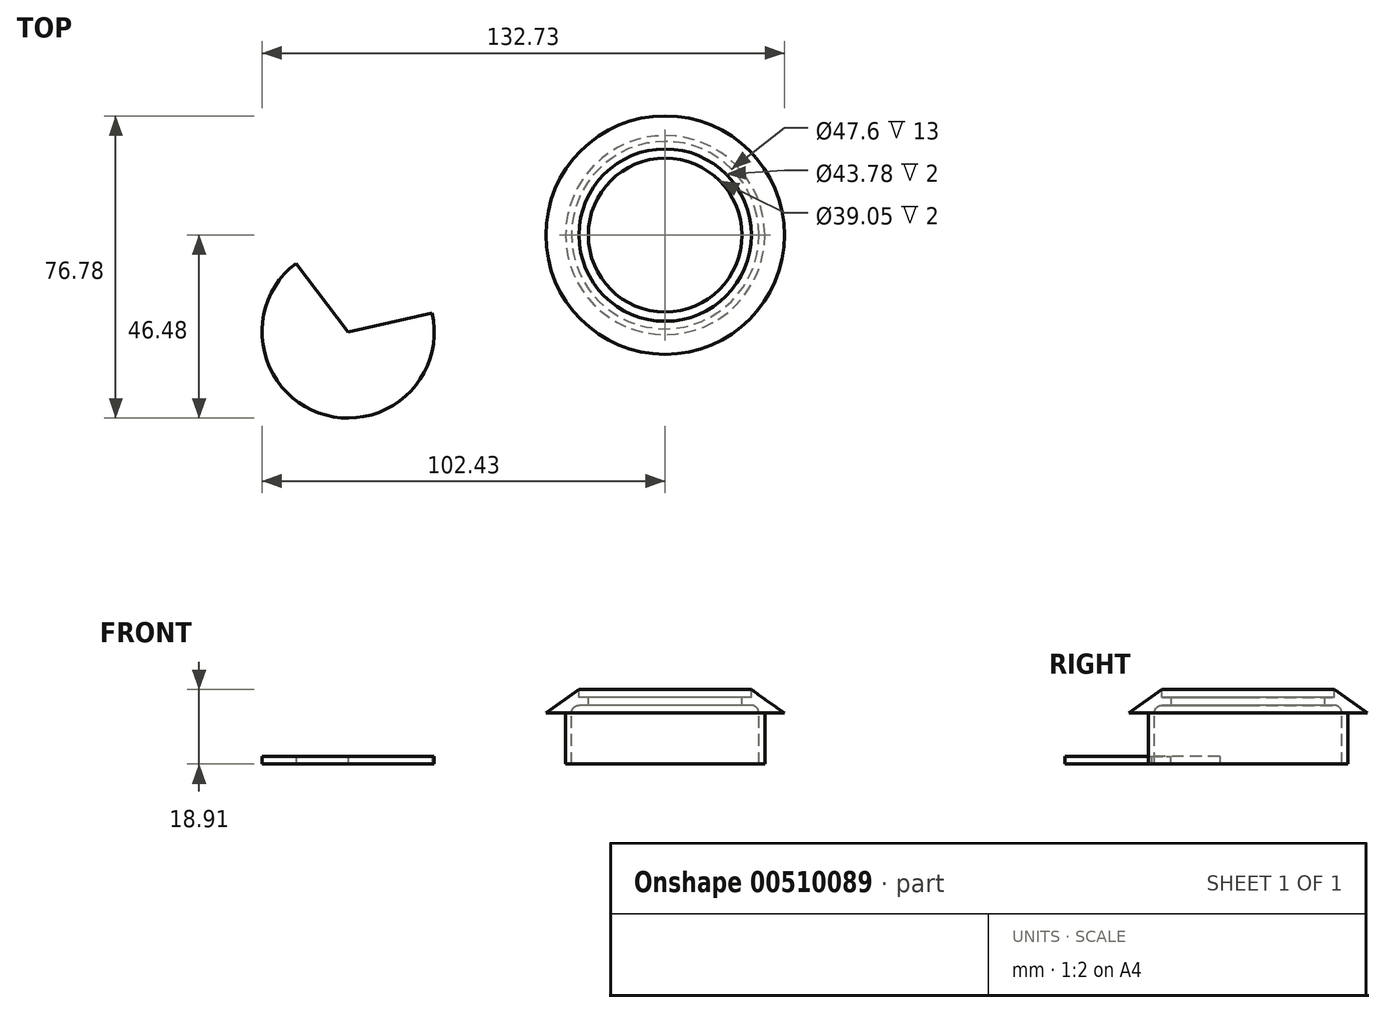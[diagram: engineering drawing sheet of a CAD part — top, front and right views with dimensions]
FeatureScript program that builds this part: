
annotation { "Feature Type Name" : "Feature", "Feature Type Description" : "" }
export const myFeature = defineFeature(function(context is Context, id is Id, definition is map)
    precondition{}
    {
        {
            var Q0;
            Q0=qCreatedBy(makeId("Front.planeOp"),FACE);
            var sketch = newSketch(context, id + "F0", { "sketchPlane" : qUnion([Q0])});
            skLineSegment(sketch, "E0", {"start": v(23.8, 0) * mm, "end": v(25.3, 0) * mm});
            skLineSegment(sketch, "E1", {"start": v(25.3, 0) * mm, "end": v(25.3, 13) * mm});
            skLineSegment(sketch, "E2", {"start": v(25.3, 13) * mm, "end": v(30.3, 13) * mm});
            skLineSegment(sketch, "E3", {"start": v(30.3, 13) * mm, "end": v(21.89, 18.91) * mm});
            skLineSegment(sketch, "E4", {"start": v(21.89, 18.91) * mm, "end": v(21.89, 16.91) * mm});
            skLineSegment(sketch, "E5", {"start": v(21.89, 16.91) * mm, "end": v(19.53, 16.91) * mm});
            skLineSegment(sketch, "E6", {"start": v(23.8, 0) * mm, "end": v(23.8, 13) * mm});
            skLineSegment(sketch, "E7", {"start": v(0, 10.58) * mm, "end": v(0, -2.42) * mm, "construction": true});
            skLineSegment(sketch, "E8", {"start": v(19.53, 16.91) * mm, "end": v(19.53, 14.91) * mm});
            skLineSegment(sketch, "E9", {"start": v(19.53, 14.91) * mm, "end": v(21.89, 14.91) * mm});
            skArc(sketch, "E10", {"start": v(23.8, 13) * mm, "mid": v(23.24, 14.35) * mm, "end": v(21.89, 14.91) * mm});
            skSolve(sketch);
        }
        {
            var Q0;
            Q0 = qSketchRegion(id + "F0", true);
            var Q1;
            Q1=sQuery(id+"F0.wireOp",EDGE,"E7");
            revolve(context, id + "F1", {"entities" : qUnion([Q0]), "axis" : qUnion([Q1]), "revolveType" : RevolveType.FULL});
        }
        {
            var Q0;
            Q0=qCreatedBy(makeId("Top.planeOp"),FACE);
            var sketch = newSketch(context, id + "F2", { "sketchPlane" : qUnion([Q0])});
            skArc(sketch, "E11", {"start": v(-93.81, -7.2) * mm, "mid": v(-88, -45.17) * mm, "end": v(-59.2, -19.74) * mm});
            skLineSegment(sketch, "E12", {"start": v(-93.81, -7.2) * mm, "end": v(-80.54, -24.6) * mm});
            skLineSegment(sketch, "E13", {"start": v(-80.54, -24.6) * mm, "end": v(-59.2, -19.74) * mm});
            skSolve(sketch);
        }
        {
            var Q0;
            Q0=makeQuery(id+"F2.imprint","IMPRINT",FACE,{"disambiguationData":[TD([[makeQuery(id+"F2.imprint","IMPRINT",EDGE,{"derivedFrom":sQuery(id+"F2.wireOp",EDGE,"E11")}),1.0]])]});
            var Q1;
            Q1 = qSketchRegion(id + "F2", true);
            extrude(context, id + "F3", {"entities" : qUnion([Q0, Q1]), "depth" : 2 * mm});
        }
    });
